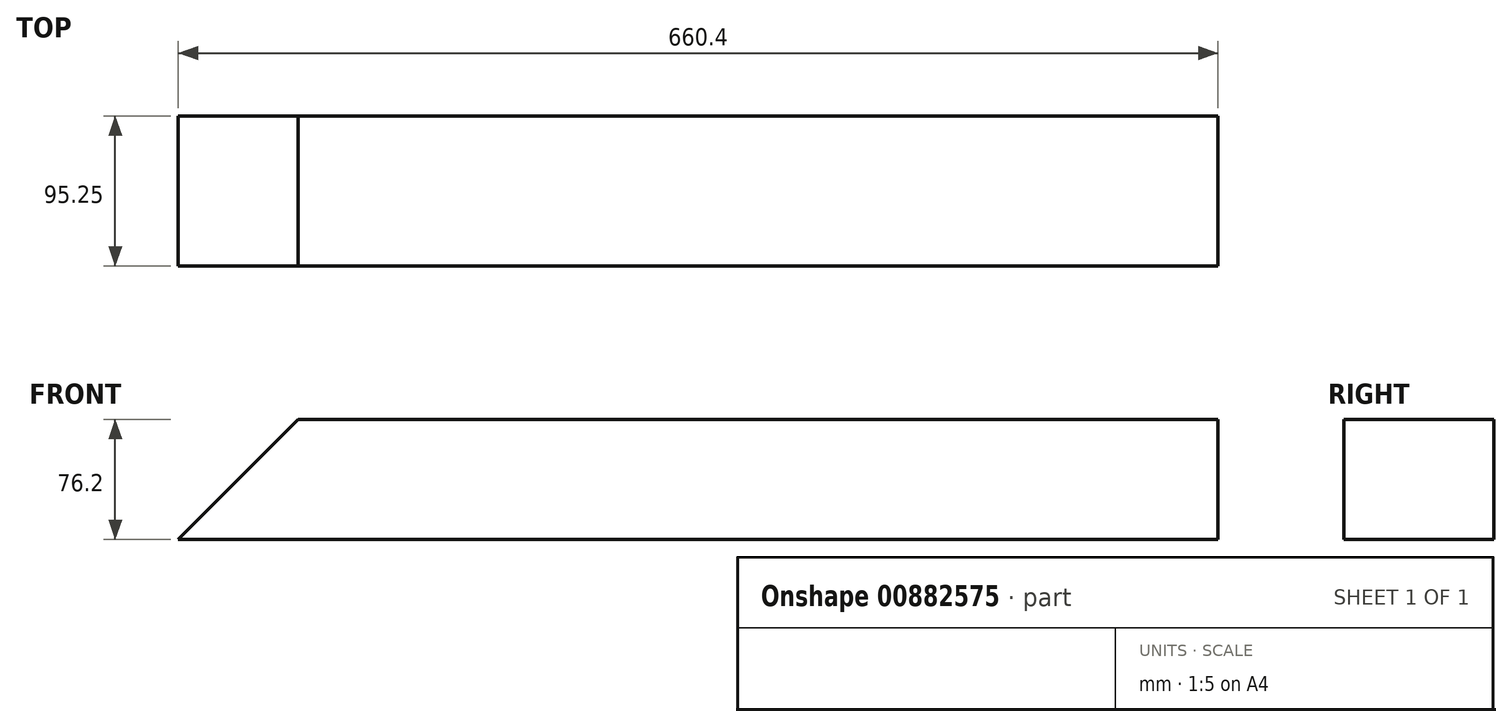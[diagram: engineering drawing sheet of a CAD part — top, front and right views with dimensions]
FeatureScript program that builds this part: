
annotation { "Feature Type Name" : "Feature", "Feature Type Description" : "" }
export const myFeature = defineFeature(function(context is Context, id is Id, definition is map)
    precondition{}
    {
        {
            var Q0;
            Q0=qCreatedBy(makeId("Right.planeOp"),FACE);
            var sketch = newSketch(context, id + "F0", { "sketchPlane" : qUnion([Q0])});
            skLineSegment(sketch, "E0.bottom", {"start": v(0, 0) * mm, "end": v(-95.25, 0) * mm});
            skLineSegment(sketch, "E0.top", {"start": v(0, -76.2) * mm, "end": v(-95.25, -76.2) * mm});
            skLineSegment(sketch, "E0.left", {"start": v(0, 0) * mm, "end": v(0, -76.2) * mm});
            skLineSegment(sketch, "E0.right", {"start": v(-95.25, 0) * mm, "end": v(-95.25, -76.2) * mm});
            skSolve(sketch);
        }
        {
            var Q0;
            Q0=makeQuery(id+"F0.imprint","IMPRINT",FACE,{"disambiguationData":[TD([[makeQuery(id+"F0.imprint","IMPRINT",EDGE,{"derivedFrom":sQuery(id+"F0.wireOp",EDGE,"E0.bottom")}),1.0]])]});
            extrude(context, id + "F1", {"entities" : qUnion([Q0]), "depth" : 660.4 * mm, "offsetDistance" : 25.4 * mm});
        }
        {
            var Q0;
            Q0=makeQuery(id+"F1.opExtrude","SWEPT_FACE",FACE,{"disambiguationData":[OSD([sQuery(id+"F0.wireOp",EDGE,"E0.right")])]});
            var sketch = newSketch(context, id + "F2", { "sketchPlane" : qUnion([Q0])});
            skLineSegment(sketch, "E1", {"start": v(0, -76.2) * mm, "end": v(0, 0) * mm});
            skLineSegment(sketch, "E2", {"start": v(0, 0) * mm, "end": v(76.2, 0) * mm});
            skLineSegment(sketch, "E3", {"start": v(76.2, 0) * mm, "end": v(0, -76.2) * mm});
            skSolve(sketch);
        }
        {
            var Q0;
            Q0 = qSketchRegion(id + "F2", true);
            extrude(context, id + "F3", {"entities" : qUnion([Q0]), "operationType" : NewBodyOperationType.REMOVE, "endBound" : BoundingType.THROUGH_ALL, "oppositeDirection" : true, "depth" : 25.4 * mm, "offsetDistance" : 25.4 * mm});
        }
    });
